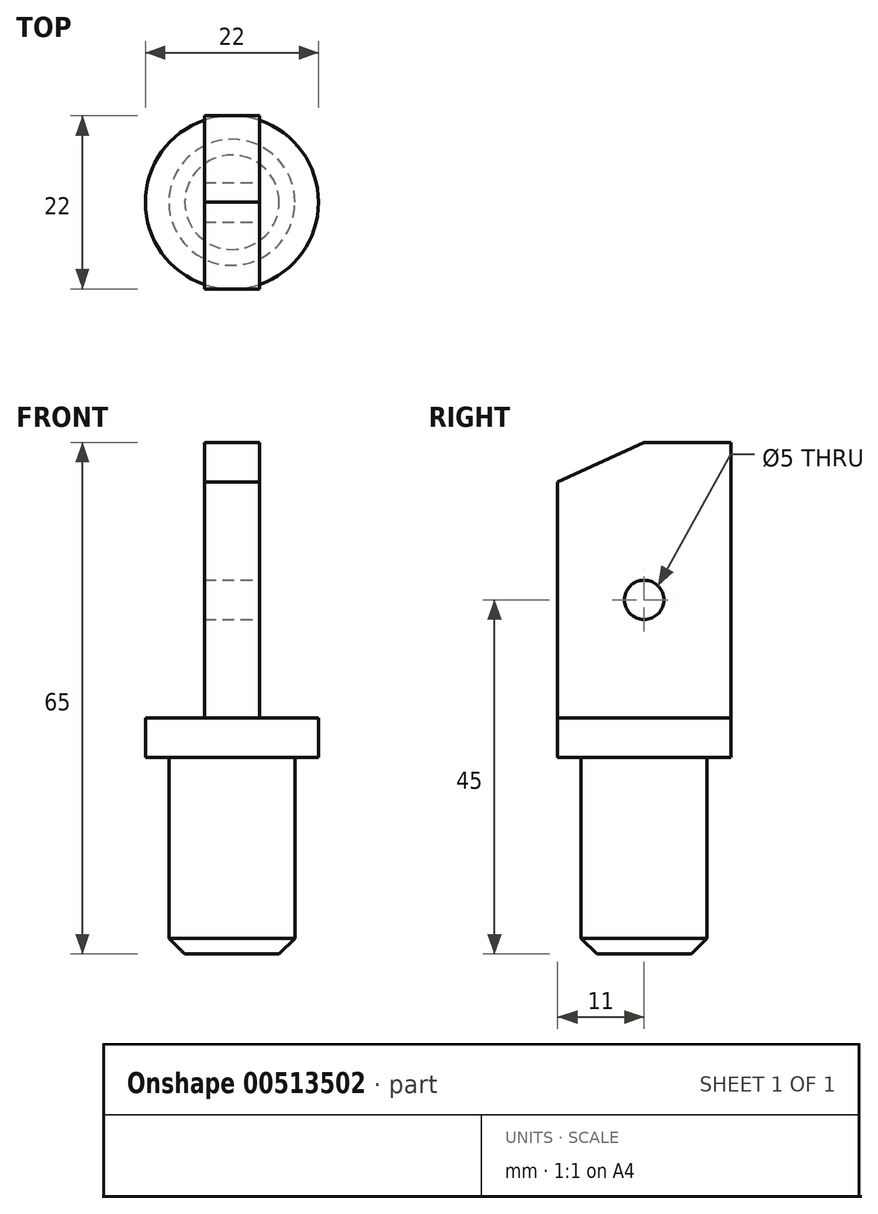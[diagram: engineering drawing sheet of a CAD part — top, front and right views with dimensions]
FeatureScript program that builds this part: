
annotation { "Feature Type Name" : "Feature", "Feature Type Description" : "" }
export const myFeature = defineFeature(function(context is Context, id is Id, definition is map)
    precondition{}
    {
        {
            var Q0;
            Q0=qCreatedBy(makeId("Top.planeOp"),FACE);
            var sketch = newSketch(context, id + "F0", { "sketchPlane" : qUnion([Q0])});
            skCircle(sketch, "E0", {"center": v(0, 0) * mm, "radius": 11 * mm});
            skSolve(sketch);
        }
        {
            var Q0;
            Q0 = qSketchRegion(id + "F0", true);
            extrude(context, id + "F1", {"entities" : qUnion([Q0]), "depth" : 5 * mm, "offsetDistance" : 25 * mm});
        }
        {
            var Q0;
            Q0=qCreatedBy(makeId("Right.planeOp"),FACE);
            var sketch = newSketch(context, id + "F2", { "sketchPlane" : qUnion([Q0])});
            skLineSegment(sketch, "E1", {"start": v(0, 0) * mm, "end": v(0, 5) * mm});
            skLineSegment(sketch, "E2", {"start": v(0, 5) * mm, "end": v(11, 5) * mm});
            skLineSegment(sketch, "E3.bottom", {"start": v(11, 5) * mm, "end": v(-11, 5) * mm});
            skLineSegment(sketch, "E3.top", {"start": v(11, 40) * mm, "end": v(-11, 40) * mm});
            skLineSegment(sketch, "E3.left", {"start": v(11, 5) * mm, "end": v(11, 40) * mm});
            skLineSegment(sketch, "E3.right", {"start": v(-11, 5) * mm, "end": v(-11, 40) * mm});
            skSolve(sketch);
        }
        {
            var Q0;
            Q0=makeQuery(id+"F2.imprint","IMPRINT",FACE,{"disambiguationData":[TD([[makeQuery(id+"F2.imprint","IMPRINT",EDGE,{"derivedFrom":sQuery(id+"F2.wireOp",EDGE,"E3.top")}),1.0]])]});
            extrude(context, id + "F3", {"entities" : qUnion([Q0]), "operationType" : NewBodyOperationType.ADD, "endBound" : BoundingType.SYMMETRIC, "depth" : 7 * mm, "offsetDistance" : 25 * mm});
        }
        {
            var Q0;
            Q0=makeQuery(id+"F3.opExtrude","CAP_FACE",FACE,{"disambiguationData":[OSD([sQuery(id+"F2.wireOp",EDGE,"E3.bottom"),sQuery(id+"F2.wireOp",EDGE,"E3.top"),sQuery(id+"F2.wireOp",EDGE,"E3.left"),sQuery(id+"F2.wireOp",EDGE,"E3.right")])],"isStart":false});
            var sketch = newSketch(context, id + "F4", { "sketchPlane" : qUnion([Q0])});
            skLineSegment(sketch, "E4", {"start": v(0, 40) * mm, "end": v(-11, 35) * mm});
            skSolve(sketch);
        }
        {
            var Q0;
            {var subQ0=sQuery(id+"F4.wireOp",EDGE,"E4");Q0=makeQuery(id+"F4.imprint","IMPRINT",FACE,{"disambiguationData":[TD([[makeQuery(id+"F4.imprint","IMPRINT",EDGE,{"derivedFrom":subQ0}),-1.0]])]});}
            extrude(context, id + "F5", {"entities" : qUnion([Q0]), "operationType" : NewBodyOperationType.REMOVE, "endBound" : BoundingType.THROUGH_ALL, "oppositeDirection" : true, "depth" : 25 * mm, "offsetDistance" : 25 * mm});
        }
        {
            var Q0;
            Q0=makeQuery(id+"F3.opExtrude","CAP_FACE",FACE,{"disambiguationData":[OSD([sQuery(id+"F2.wireOp",EDGE,"E3.bottom"),sQuery(id+"F2.wireOp",EDGE,"E3.top"),sQuery(id+"F2.wireOp",EDGE,"E3.left"),sQuery(id+"F2.wireOp",EDGE,"E3.right")])],"isStart":false});
            var sketch = newSketch(context, id + "F6", { "sketchPlane" : qUnion([Q0])});
            skCircle(sketch, "E5", {"center": v(0, 20) * mm, "radius": 2.5 * mm});
            skSolve(sketch);
        }
        {
            var Q0;
            Q0 = qSketchRegion(id + "F6", true);
            extrude(context, id + "F7", {"entities" : qUnion([Q0]), "operationType" : NewBodyOperationType.REMOVE, "endBound" : BoundingType.THROUGH_ALL, "oppositeDirection" : true, "depth" : 25 * mm, "offsetDistance" : 25 * mm});
        }
        {
            var Q0;
            Q0=makeQuery(id+"F1.opExtrude","CAP_FACE",FACE,{"disambiguationData":[OSD([sQuery(id+"F0.wireOp",EDGE,"E0")])],"isStart":true});
            var sketch = newSketch(context, id + "F8", { "sketchPlane" : qUnion([Q0])});
            skCircle(sketch, "E6", {"center": v(0, 0) * mm, "radius": 8 * mm});
            skSolve(sketch);
        }
        {
            var Q0;
            Q0 = qSketchRegion(id + "F8", true);
            extrude(context, id + "F9", {"entities" : qUnion([Q0]), "operationType" : NewBodyOperationType.ADD, "depth" : 25 * mm, "offsetDistance" : 25 * mm});
        }
        {
            var Q0;
            Q0=makeQuery(id+"F9.opExtrude","CAP_FACE",FACE,{"disambiguationData":[OSD([sQuery(id+"F8.wireOp",EDGE,"E6")])],"isStart":false});
            chamfer(context, id + "F10", {"entities" : qUnion([Q0]), "width" : 2 * mm, "tangentPropagation" : true});
        }
    });
